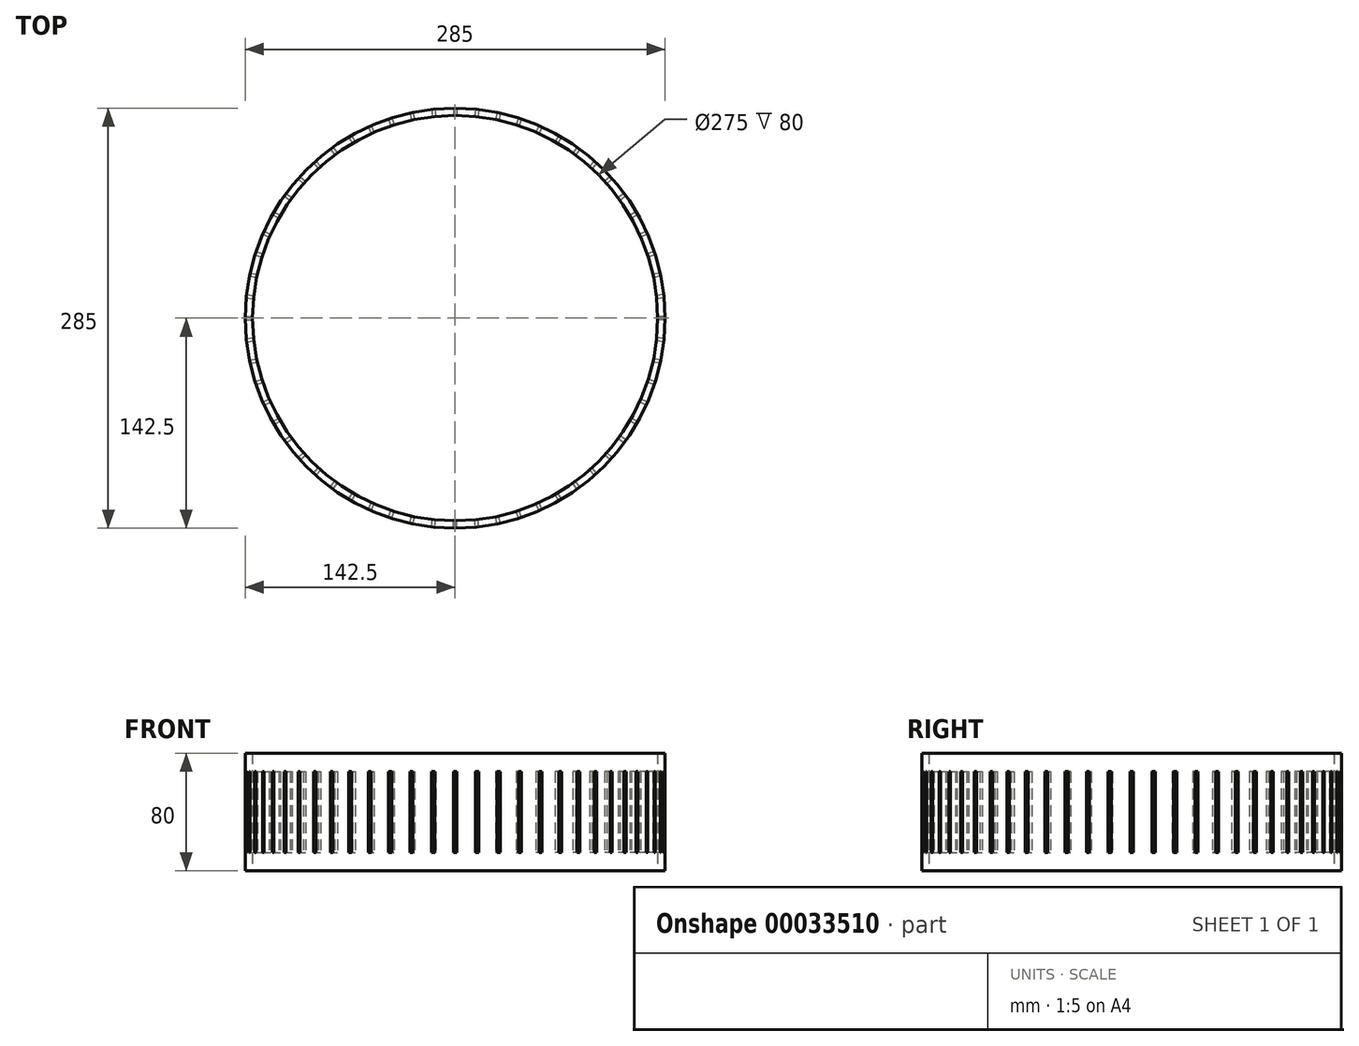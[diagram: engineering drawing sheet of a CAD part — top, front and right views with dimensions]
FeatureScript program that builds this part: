
annotation { "Feature Type Name" : "Feature", "Feature Type Description" : "" }
export const myFeature = defineFeature(function(context is Context, id is Id, definition is map)
    precondition{}
    {
        {
            var Q0;
            Q0=qCreatedBy(makeId("Top.planeOp"),FACE);
            var sketch = newSketch(context, id + "F0", { "sketchPlane" : qUnion([Q0])});
            skCircle(sketch, "E0", {"center": v(0, 0) * mm, "radius": 142.5 * mm});
            skCircle(sketch, "E1", {"center": v(0, 0) * mm, "radius": 137.5 * mm});
            skSolve(sketch);
        }
        {
            var Q0;
            Q0 = qSketchRegion(id + "F0", true);
            extrude(context, id + "F1", {"entities" : qUnion([Q0]), "depth" : 80 * mm});
        }
        {
            var Q0;
            Q0=qCreatedBy(makeId("Front.planeOp"),FACE);
            var sketch = newSketch(context, id + "F2", { "sketchPlane" : qUnion([Q0])});
            skLineSegment(sketch, "E2.rect.bottom", {"start": v(-1.1, 12.5) * mm, "end": v(1.1, 12.5) * mm});
            skLineSegment(sketch, "E2.rect.top", {"start": v(-1.1, 67.5) * mm, "end": v(1.1, 67.5) * mm});
            skLineSegment(sketch, "E2.rect.left", {"start": v(-1.1, 12.5) * mm, "end": v(-1.1, 67.5) * mm});
            skLineSegment(sketch, "E2.rect.right", {"start": v(1.1, 12.5) * mm, "end": v(1.1, 67.5) * mm});
            skPoint(sketch, "E2.rect.middle", {"position": v(0, 40) * mm});
            skLineSegment(sketch, "E3", {"start": v(0, 0) * mm, "end": v(0, -105.1) * mm, "construction": true});
            skSolve(sketch);
        }
        {
            var Q0;
            Q0 = qSketchRegion(id + "F2", true);
            extrude(context, id + "F3", {"entities" : qUnion([Q0]), "operationType" : NewBodyOperationType.REMOVE, "endBound" : BoundingType.THROUGH_ALL, "oppositeDirection" : true, "depth" : 25 * mm});
        }
        {
            var Q0;
            Q0=makeQuery(id+"F3.boolean.opBoolean","COPY",FACE,{"derivedFrom":makeQuery(id+"F3.opExtrude","SWEPT_FACE",FACE,{"disambiguationData":[OSD([sQuery(id+"F2.wireOp",EDGE,"E2.rect.right")])]})});
            var Q1;
            Q1=makeQuery(id+"F3.boolean.opBoolean","COPY",FACE,{"derivedFrom":makeQuery(id+"F3.opExtrude","SWEPT_FACE",FACE,{"disambiguationData":[OSD([sQuery(id+"F2.wireOp",EDGE,"E2.rect.bottom")])]})});
            var Q2;
            Q2=makeQuery(id+"F3.boolean.opBoolean","COPY",FACE,{"derivedFrom":makeQuery(id+"F3.opExtrude","SWEPT_FACE",FACE,{"disambiguationData":[OSD([sQuery(id+"F2.wireOp",EDGE,"E2.rect.left")])]})});
            var Q3;
            Q3=makeQuery(id+"F3.boolean.opBoolean","COPY",FACE,{"derivedFrom":makeQuery(id+"F3.opExtrude","SWEPT_FACE",FACE,{"disambiguationData":[OSD([sQuery(id+"F2.wireOp",EDGE,"E2.rect.top")])]})});
            var Q4;
            Q4=sQuery(id+"F2.wireOp",EDGE,"E3");
            circularPattern(context, id + "F4", {"faces" : qUnion([Q0, Q1, Q2, Q3]), "axis" : qUnion([Q4]), "angle" : 6 * degree, "instanceCount" : 60, "patternType" : PatternType.FACE});
        }
    });
